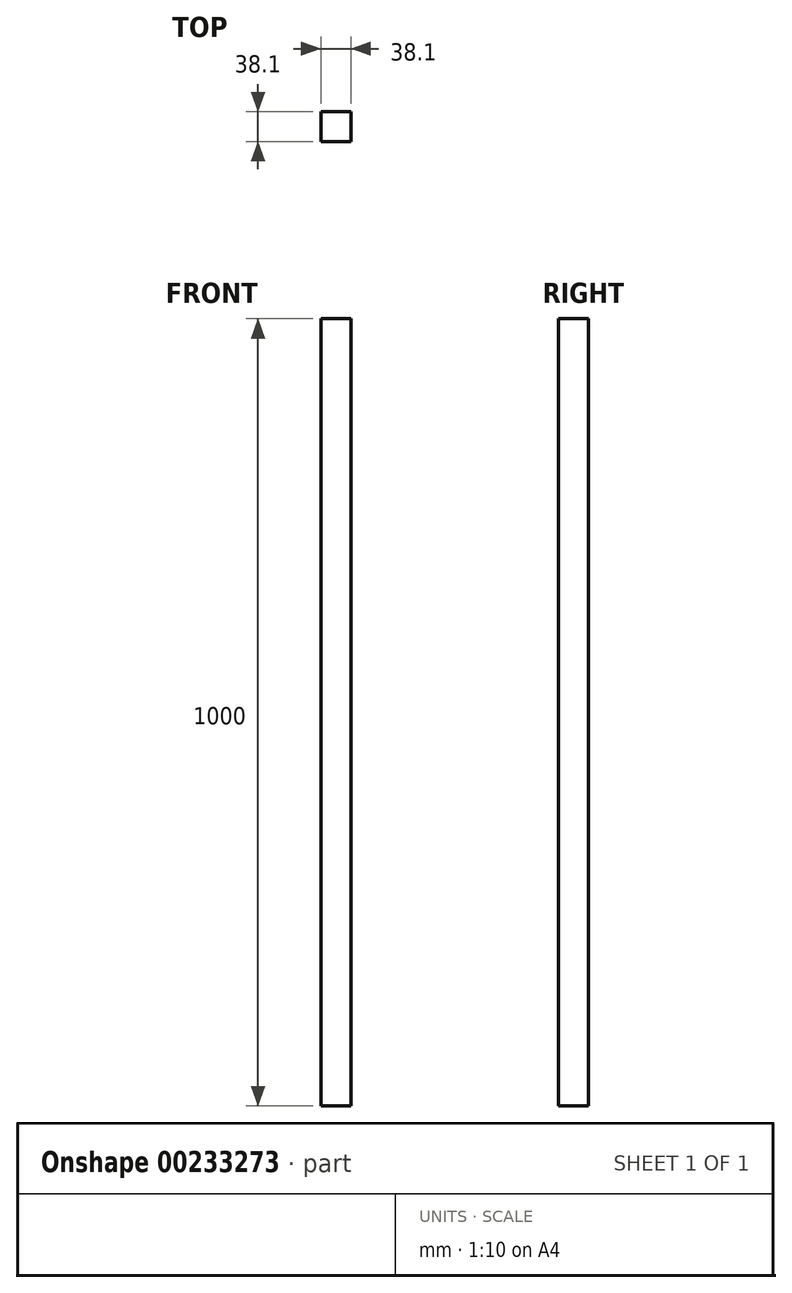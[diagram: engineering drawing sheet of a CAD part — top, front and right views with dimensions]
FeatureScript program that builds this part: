
annotation { "Feature Type Name" : "Feature", "Feature Type Description" : "" }
export const myFeature = defineFeature(function(context is Context, id is Id, definition is map)
    precondition{}
    {
        {
            var Q0;
            Q0=qCreatedBy(makeId("Front.planeOp"),FACE);
            var sketch = newSketch(context, id + "F0", { "sketchPlane" : qUnion([Q0])});
            skLineSegment(sketch, "E0.bottom", {"start": v(-789.82, 525.65) * mm, "end": v(-751.72, 525.65) * mm});
            skLineSegment(sketch, "E0.top", {"start": v(-789.82, -474.35) * mm, "end": v(-751.72, -474.35) * mm});
            skLineSegment(sketch, "E0.left", {"start": v(-789.82, 525.65) * mm, "end": v(-789.82, -474.35) * mm});
            skLineSegment(sketch, "E0.right", {"start": v(-751.72, 525.65) * mm, "end": v(-751.72, -474.35) * mm});
            skSolve(sketch);
        }
        {
            var Q0;
            Q0=makeQuery(id+"F0.imprint","IMPRINT",FACE,{"disambiguationData":[TD([[makeQuery(id+"F0.imprint","IMPRINT",EDGE,{"derivedFrom":sQuery(id+"F0.wireOp",EDGE,"E0.bottom")}),-1.0]])]});
            extrude(context, id + "F1", {"entities" : qUnion([Q0]), "depth" : 38.1 * mm});
        }
    });
